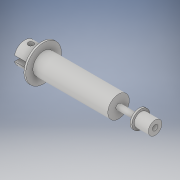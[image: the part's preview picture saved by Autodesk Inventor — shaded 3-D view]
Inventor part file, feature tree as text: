
AUTODESK INVENTOR PART (.ipt)
format: ipt  version: 2017 (Build 210142000, 142)  size: 171,520 bytes
history: native  units: in
note: dims shown in document units (in); Inventor stores cm internally (conversion verified against a paired STEP export)
features: extrude x11, sketch x11
ambient origin geometry x8: Origin, YZ Plane, XZ Plane, XY Plane, X Axis, Y Axis, Z Axis, Center Point
bodies: Solid1 (feature_tree)
feature tree (22):
  extrude  "Extrusion1"  Depth=2.0669in TaperAngle=0.0deg
  extrude  "Extrusion2"  Depth=0.4528in TaperAngle=0.0deg
  extrude  "Extrusion3"  Depth=0.3937in TaperAngle=0.0deg
  extrude  "Extrusion4"  Depth=0.315in TaperAngle=0.0deg
  extrude  "Extrusion5"  Depth=0.315in TaperAngle=0.0deg
  extrude  "Extrusion6"  Depth=0.4724in
  extrude  "Extrusion7"  Depth=0.7874in
  extrude  "Extrusion8"  Depth=0.4724in
  extrude  "Extrusion10"  Depth=0.374in TaperAngle=0.0deg
  extrude  "Extrusion12"  Depth=0.3543in TaperAngle=0.0deg
  extrude  "Extrusion13"  Depth=0.3937in
  sketch  "Sketch1"  dims[d0=0.4724in d1=2.0669in d2=0.0in]
  sketch  "Sketch2"  dims[d3=0.1181in d4=0.4528in d5=0.0in]
  sketch  "Sketch3"  dims[d6=0.3937in d7=0.0394in d8=0.0in]
  sketch  "Sketch4"  dims[d9=0.2953in d10=0.315in d11=0.0in]
  sketch  "Sketch5"  dims[d12=0.1181in d13=0.315in d14=0.0in]
  sketch  "Sketch6"  dims[d15=0.4331in d16=0.4724in]
  sketch  "Sketch7"  dims[d17=0.4134in d18=0.0in d19=0.7874in]
  sketch  "Sketch8"  dims[d20=0.0394in d21=0.0in d23=0.4724in]
  sketch  "Sketch10"  dims[d24=0.3543in d25=0.0in d31=0.374in d32=0.0in]
  sketch  "Sketch12"  dims[d35=0.1181in d36=0.3543in d37=0.0in]
  sketch  "Sketch13"  dims[d38=0.2756in d39=0.1181in d40=0.3937in d41=0.0in]
